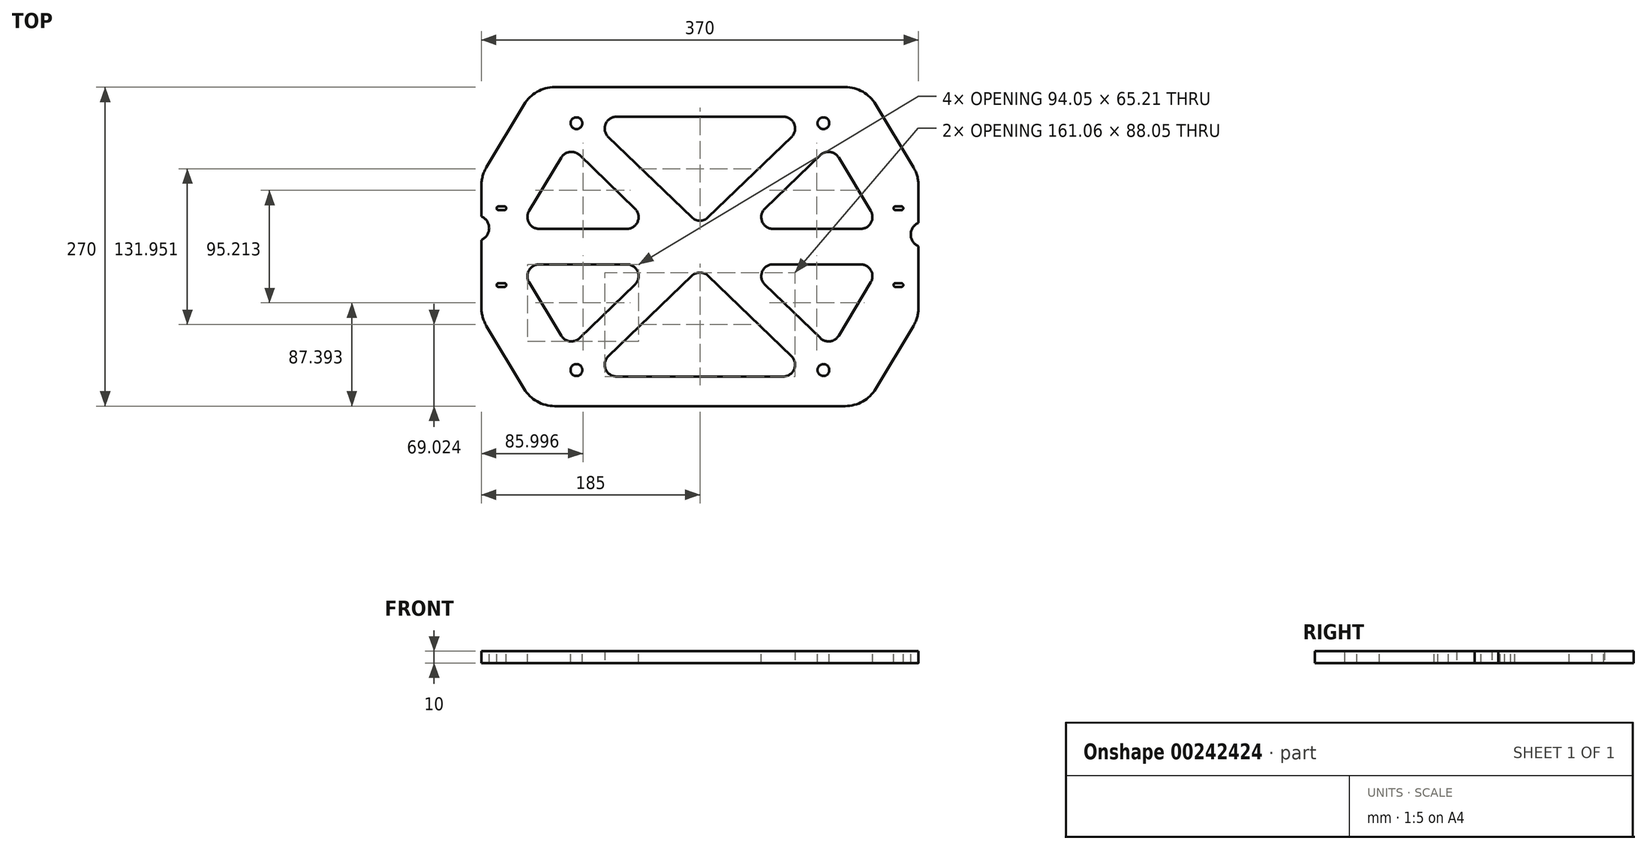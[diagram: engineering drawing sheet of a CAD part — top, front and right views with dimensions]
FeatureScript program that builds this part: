
annotation { "Feature Type Name" : "Feature", "Feature Type Description" : "" }
export const myFeature = defineFeature(function(context is Context, id is Id, definition is map)
    precondition{}
    {
        {
            var Q0;
            Q0=qCreatedBy(makeId("Top.planeOp"),FACE);
            var sketch = newSketch(context, id + "F0", { "sketchPlane" : qUnion([Q0])});
            skLineSegment(sketch, "E0.bottom", {"start": v(185, 135) * mm, "end": v(-185, 135) * mm, "construction": true});
            skLineSegment(sketch, "E0.top", {"start": v(185, -135) * mm, "end": v(-185, -135) * mm, "construction": true});
            skLineSegment(sketch, "E0.left", {"start": v(185, 135) * mm, "end": v(185, -135) * mm, "construction": true});
            skLineSegment(sketch, "E0.right", {"start": v(-185, 135) * mm, "end": v(-185, -135) * mm, "construction": true});
            skPoint(sketch, "E0.middle", {"position": v(0, 0) * mm});
            skLineSegment(sketch, "E1", {"start": v(-140, 135) * mm, "end": v(140, 135) * mm});
            skLineSegment(sketch, "E2", {"start": v(-140, -135) * mm, "end": v(140, -135) * mm});
            skLineSegment(sketch, "E3", {"start": v(-185, 60) * mm, "end": v(-185, -60) * mm});
            skLineSegment(sketch, "E4", {"start": v(185, 60) * mm, "end": v(185, -60) * mm});
            skLineSegment(sketch, "E5", {"start": v(-140, 135) * mm, "end": v(-185, 60) * mm});
            skLineSegment(sketch, "E6", {"start": v(140, 135) * mm, "end": v(185, 60) * mm});
            skLineSegment(sketch, "E7", {"start": v(140, -135) * mm, "end": v(185, -60) * mm});
            skLineSegment(sketch, "E8", {"start": v(-140, -135) * mm, "end": v(-185, -60) * mm});
            skLineSegment(sketch, "E9", {"start": v(-140, 135) * mm, "end": v(140, -135) * mm, "construction": true});
            skLineSegment(sketch, "E10", {"start": v(140, 135) * mm, "end": v(-140, -135) * mm, "construction": true});
            skLineSegment(sketch, "E11", {"start": v(-95.35, -110) * mm, "end": v(0, -18.06) * mm});
            skLineSegment(sketch, "E12", {"start": v(0, -18.06) * mm, "end": v(95.35, -110) * mm});
            skLineSegment(sketch, "E13", {"start": v(-95.35, 110) * mm, "end": v(0, 18.06) * mm});
            skLineSegment(sketch, "E14", {"start": v(0, 18.06) * mm, "end": v(95.35, 110) * mm});
            skLineSegment(sketch, "E15", {"start": v(-185, 0) * mm, "end": v(185, 0) * mm, "construction": true});
            skLineSegment(sketch, "E16", {"start": v(110.98, 86.18) * mm, "end": v(37.17, 15) * mm});
            skLineSegment(sketch, "E17", {"start": v(37.17, 15) * mm, "end": v(153.7, 15) * mm});
            skLineSegment(sketch, "E18", {"start": v(153.7, 15) * mm, "end": v(110.98, 86.18) * mm});
            skLineSegment(sketch, "E19", {"start": v(153.7, -15) * mm, "end": v(37.17, -15) * mm});
            skLineSegment(sketch, "E20", {"start": v(37.17, -15) * mm, "end": v(110.98, -86.18) * mm});
            skLineSegment(sketch, "E21", {"start": v(110.98, -86.18) * mm, "end": v(153.7, -15) * mm});
            skLineSegment(sketch, "E22", {"start": v(-110.98, 86.18) * mm, "end": v(-37.17, 15) * mm});
            skLineSegment(sketch, "E23", {"start": v(-37.17, 15) * mm, "end": v(-153.7, 15) * mm});
            skLineSegment(sketch, "E24", {"start": v(-153.7, 15) * mm, "end": v(-110.98, 86.18) * mm});
            skLineSegment(sketch, "E25", {"start": v(-153.7, -15) * mm, "end": v(-37.17, -15) * mm});
            skLineSegment(sketch, "E26", {"start": v(-37.17, -15) * mm, "end": v(-110.98, -86.18) * mm});
            skLineSegment(sketch, "E27", {"start": v(-110.98, -86.18) * mm, "end": v(-153.7, -15) * mm});
            skLineSegment(sketch, "E28", {"start": v(-95.35, 110) * mm, "end": v(95.35, 110) * mm});
            skLineSegment(sketch, "E29", {"start": v(-95.35, -110) * mm, "end": v(95.35, -110) * mm});
            skLineSegment(sketch, "E30", {"start": v(153.7, -15) * mm, "end": v(153.7, 15) * mm, "construction": true});
            skLineSegment(sketch, "E31", {"start": v(110.98, 86.18) * mm, "end": v(110.98, -86.18) * mm, "construction": true});
            skLineSegment(sketch, "E32", {"start": v(-110.98, 86.18) * mm, "end": v(-110.98, -86.18) * mm, "construction": true});
            skLineSegment(sketch, "E33", {"start": v(-153.7, 15) * mm, "end": v(-153.7, -15) * mm, "construction": true});
            skLineSegment(sketch, "E34", {"start": v(-37.17, 15) * mm, "end": v(37.17, 15) * mm, "construction": true});
            skLineSegment(sketch, "E35", {"start": v(-37.17, -15) * mm, "end": v(37.17, -15) * mm, "construction": true});
            skLineSegment(sketch, "E36", {"start": v(37.17, 15) * mm, "end": v(37.17, -15) * mm, "construction": true});
            skLineSegment(sketch, "E37", {"start": v(-37.17, 15) * mm, "end": v(-37.17, -15) * mm, "construction": true});
            skLineSegment(sketch, "E38", {"start": v(-110.98, 86.18) * mm, "end": v(110.98, 86.18) * mm, "construction": true});
            skPoint(sketch, "E39", {"position": v(0, -15) * mm});
            skLineSegment(sketch, "E40", {"start": v(95.35, 110) * mm, "end": v(95.35, -110) * mm, "construction": true});
            skLineSegment(sketch, "E41", {"start": v(-95.35, 110) * mm, "end": v(-95.35, -110) * mm, "construction": true});
            skLineSegment(sketch, "E42", {"start": v(0, 18.06) * mm, "end": v(0, -18.06) * mm, "construction": true});
            skPoint(sketch, "E43", {"position": v(-153.7, 0) * mm});
            skSolve(sketch);
        }
        {
            var Q0;
            Q0=makeQuery(id+"F0.imprint","IMPRINT",FACE,{"disambiguationData":[TD([[makeQuery(id+"F0.imprint","IMPRINT",EDGE,{"derivedFrom":sQuery(id+"F0.wireOp",EDGE,"E1")}),-1.0]])]});
            extrude(context, id + "F1", {"entities" : qUnion([Q0]), "depth" : 10 * mm});
        }
        {
            var Q0;
            Q0=makeQuery(id+"F1.opExtrude","SWEPT_EDGE",EDGE,{"disambiguationData":[OSD([sQuery(id+"F0.wireOp",EDGE,"E22"),sQuery(id+"F0.wireOp",EDGE,"E24")])]});
            var Q1;
            Q1=makeQuery(id+"F1.opExtrude","SWEPT_EDGE",EDGE,{"disambiguationData":[OSD([sQuery(id+"F0.wireOp",EDGE,"E23"),sQuery(id+"F0.wireOp",EDGE,"E24")])]});
            var Q2;
            Q2=makeQuery(id+"F1.opExtrude","SWEPT_EDGE",EDGE,{"disambiguationData":[OSD([sQuery(id+"F0.wireOp",EDGE,"E22"),sQuery(id+"F0.wireOp",EDGE,"E23")])]});
            var Q3;
            Q3=makeQuery(id+"F1.opExtrude","SWEPT_EDGE",EDGE,{"disambiguationData":[OSD([sQuery(id+"F0.wireOp",EDGE,"E17"),sQuery(id+"F0.wireOp",EDGE,"E18")])]});
            var Q4;
            Q4=makeQuery(id+"F1.opExtrude","SWEPT_EDGE",EDGE,{"disambiguationData":[OSD([sQuery(id+"F0.wireOp",EDGE,"E13"),sQuery(id+"F0.wireOp",EDGE,"E14")])]});
            var Q5;
            Q5=makeQuery(id+"F1.opExtrude","SWEPT_EDGE",EDGE,{"disambiguationData":[OSD([sQuery(id+"F0.wireOp",EDGE,"E13"),sQuery(id+"F0.wireOp",EDGE,"E28")])]});
            var Q6;
            Q6=makeQuery(id+"F1.opExtrude","SWEPT_EDGE",EDGE,{"disambiguationData":[OSD([sQuery(id+"F0.wireOp",EDGE,"E14"),sQuery(id+"F0.wireOp",EDGE,"E28")])]});
            var Q7;
            Q7=makeQuery(id+"F1.opExtrude","SWEPT_EDGE",EDGE,{"disambiguationData":[OSD([sQuery(id+"F0.wireOp",EDGE,"E25"),sQuery(id+"F0.wireOp",EDGE,"E27")])]});
            var Q8;
            Q8=makeQuery(id+"F1.opExtrude","SWEPT_EDGE",EDGE,{"disambiguationData":[OSD([sQuery(id+"F0.wireOp",EDGE,"E25"),sQuery(id+"F0.wireOp",EDGE,"E26")])]});
            var Q9;
            Q9=makeQuery(id+"F1.opExtrude","SWEPT_EDGE",EDGE,{"disambiguationData":[OSD([sQuery(id+"F0.wireOp",EDGE,"E26"),sQuery(id+"F0.wireOp",EDGE,"E27")])]});
            var Q10;
            Q10=makeQuery(id+"F1.opExtrude","SWEPT_EDGE",EDGE,{"disambiguationData":[OSD([sQuery(id+"F0.wireOp",EDGE,"E11"),sQuery(id+"F0.wireOp",EDGE,"E12")])]});
            var Q11;
            Q11=makeQuery(id+"F1.opExtrude","SWEPT_EDGE",EDGE,{"disambiguationData":[OSD([sQuery(id+"F0.wireOp",EDGE,"E11"),sQuery(id+"F0.wireOp",EDGE,"E29")])]});
            var Q12;
            Q12=makeQuery(id+"F1.opExtrude","SWEPT_EDGE",EDGE,{"disambiguationData":[OSD([sQuery(id+"F0.wireOp",EDGE,"E12"),sQuery(id+"F0.wireOp",EDGE,"E29")])]});
            var Q13;
            Q13=makeQuery(id+"F1.opExtrude","SWEPT_EDGE",EDGE,{"disambiguationData":[OSD([sQuery(id+"F0.wireOp",EDGE,"E19"),sQuery(id+"F0.wireOp",EDGE,"E21")])]});
            var Q14;
            Q14=makeQuery(id+"F1.opExtrude","SWEPT_EDGE",EDGE,{"disambiguationData":[OSD([sQuery(id+"F0.wireOp",EDGE,"E19"),sQuery(id+"F0.wireOp",EDGE,"E20")])]});
            var Q15;
            Q15=makeQuery(id+"F1.opExtrude","SWEPT_EDGE",EDGE,{"disambiguationData":[OSD([sQuery(id+"F0.wireOp",EDGE,"E20"),sQuery(id+"F0.wireOp",EDGE,"E21")])]});
            var Q16;
            Q16=makeQuery(id+"F1.opExtrude","SWEPT_EDGE",EDGE,{"disambiguationData":[OSD([sQuery(id+"F0.wireOp",EDGE,"E16"),sQuery(id+"F0.wireOp",EDGE,"E18")])]});
            var Q17;
            Q17=makeQuery(id+"F1.opExtrude","SWEPT_EDGE",EDGE,{"disambiguationData":[OSD([sQuery(id+"F0.wireOp",EDGE,"E16"),sQuery(id+"F0.wireOp",EDGE,"E17")])]});
            fillet(context, id + "F2", {"entities" : qUnion([Q0, Q1, Q2, Q3, Q4, Q5, Q6, Q7, Q8, Q9, Q10, Q11, Q12, Q13, Q14, Q15, Q16, Q17]), "radius" : 10 * mm, "tangentPropagation" : true, "allowEdgeOverflow" : false});
        }
        {
            var Q0;
            Q0=makeQuery(id+"F1.opExtrude","SWEPT_EDGE",EDGE,{"disambiguationData":[OSD([sQuery(id+"F0.wireOp",EDGE,"E3"),sQuery(id+"F0.wireOp",EDGE,"E5")])]});
            var Q1;
            Q1=makeQuery(id+"F1.opExtrude","SWEPT_EDGE",EDGE,{"disambiguationData":[OSD([sQuery(id+"F0.wireOp",EDGE,"E1"),sQuery(id+"F0.wireOp",EDGE,"E5")])]});
            var Q2;
            Q2=makeQuery(id+"F1.opExtrude","SWEPT_EDGE",EDGE,{"disambiguationData":[OSD([sQuery(id+"F0.wireOp",EDGE,"E3"),sQuery(id+"F0.wireOp",EDGE,"E8")])]});
            var Q3;
            Q3=makeQuery(id+"F1.opExtrude","SWEPT_EDGE",EDGE,{"disambiguationData":[OSD([sQuery(id+"F0.wireOp",EDGE,"E2"),sQuery(id+"F0.wireOp",EDGE,"E8")])]});
            var Q4;
            Q4=makeQuery(id+"F1.opExtrude","SWEPT_EDGE",EDGE,{"disambiguationData":[OSD([sQuery(id+"F0.wireOp",EDGE,"E2"),sQuery(id+"F0.wireOp",EDGE,"E7")])]});
            var Q5;
            Q5=makeQuery(id+"F1.opExtrude","SWEPT_EDGE",EDGE,{"disambiguationData":[OSD([sQuery(id+"F0.wireOp",EDGE,"E4"),sQuery(id+"F0.wireOp",EDGE,"E7")])]});
            var Q6;
            Q6=makeQuery(id+"F1.opExtrude","SWEPT_EDGE",EDGE,{"disambiguationData":[OSD([sQuery(id+"F0.wireOp",EDGE,"E4"),sQuery(id+"F0.wireOp",EDGE,"E6")])]});
            var Q7;
            Q7=makeQuery(id+"F1.opExtrude","SWEPT_EDGE",EDGE,{"disambiguationData":[OSD([sQuery(id+"F0.wireOp",EDGE,"E1"),sQuery(id+"F0.wireOp",EDGE,"E6")])]});
            fillet(context, id + "F3", {"entities" : qUnion([Q0, Q1, Q2, Q3, Q4, Q5, Q6, Q7]), "radius" : 30 * mm, "tangentPropagation" : true, "allowEdgeOverflow" : false});
        }
        {
            var Q0;
            Q0=makeQuery(id+"F1.opExtrude","CAP_FACE",FACE,{"disambiguationData":[OSD([sQuery(id+"F0.wireOp",EDGE,"E1"),sQuery(id+"F0.wireOp",EDGE,"E2"),sQuery(id+"F0.wireOp",EDGE,"E3"),sQuery(id+"F0.wireOp",EDGE,"E4"),sQuery(id+"F0.wireOp",EDGE,"E5"),sQuery(id+"F0.wireOp",EDGE,"E6"),sQuery(id+"F0.wireOp",EDGE,"E7"),sQuery(id+"F0.wireOp",EDGE,"E8"),sQuery(id+"F0.wireOp",EDGE,"E11"),sQuery(id+"F0.wireOp",EDGE,"E12"),sQuery(id+"F0.wireOp",EDGE,"E13"),sQuery(id+"F0.wireOp",EDGE,"E14"),sQuery(id+"F0.wireOp",EDGE,"E16"),sQuery(id+"F0.wireOp",EDGE,"E17"),sQuery(id+"F0.wireOp",EDGE,"E18"),sQuery(id+"F0.wireOp",EDGE,"E19"),sQuery(id+"F0.wireOp",EDGE,"E20"),sQuery(id+"F0.wireOp",EDGE,"E21"),sQuery(id+"F0.wireOp",EDGE,"E22"),sQuery(id+"F0.wireOp",EDGE,"E23"),sQuery(id+"F0.wireOp",EDGE,"E24"),sQuery(id+"F0.wireOp",EDGE,"E25"),sQuery(id+"F0.wireOp",EDGE,"E26"),sQuery(id+"F0.wireOp",EDGE,"E27"),sQuery(id+"F0.wireOp",EDGE,"E28"),sQuery(id+"F0.wireOp",EDGE,"E29")])],"isStart":false});
            var sketch = newSketch(context, id + "F4", { "sketchPlane" : qUnion([Q0])});
            skLineSegment(sketch, "E44.bottom", {"start": v(168, 32.5) * mm, "end": v(-168, 32.5) * mm, "construction": true});
            skLineSegment(sketch, "E44.top", {"start": v(168, -32.5) * mm, "end": v(-168, -32.5) * mm, "construction": true});
            skLineSegment(sketch, "E44.left", {"start": v(168, 32.5) * mm, "end": v(168, -32.5) * mm, "construction": true});
            skLineSegment(sketch, "E44.right", {"start": v(-168, 32.5) * mm, "end": v(-168, -32.5) * mm, "construction": true});
            skPoint(sketch, "E44.middle", {"position": v(0, 0) * mm});
            skLineSegment(sketch, "E45", {"start": v(-170.5, -32.5) * mm, "end": v(-165.5, -32.5) * mm, "construction": true});
            skPoint(sketch, "E46", {"position": v(-168, -32.5) * mm});
            skArc(sketch, "E47.0.startCap", {"start": v(-170.5, -34.1) * mm, "mid": v(-172.1, -32.5) * mm, "end": v(-170.5, -30.9) * mm});
            skArc(sketch, "E47.0.endCap", {"start": v(-165.5, -30.9) * mm, "mid": v(-163.9, -32.5) * mm, "end": v(-165.5, -34.1) * mm});
            skLineSegment(sketch, "E47.0.left", {"start": v(-170.5, -30.9) * mm, "end": v(-165.5, -30.9) * mm});
            skLineSegment(sketch, "E47.0.right", {"start": v(-170.5, -34.1) * mm, "end": v(-165.5, -34.1) * mm});
            skLineSegment(sketch, "E48", {"start": v(165.5, -32.5) * mm, "end": v(170.5, -32.5) * mm, "construction": true});
            skPoint(sketch, "E49", {"position": v(168, -32.5) * mm});
            skArc(sketch, "E50.0.startCap", {"start": v(165.5, -34.1) * mm, "mid": v(163.9, -32.5) * mm, "end": v(165.5, -30.9) * mm});
            skArc(sketch, "E50.0.endCap", {"start": v(170.5, -30.9) * mm, "mid": v(172.1, -32.5) * mm, "end": v(170.5, -34.1) * mm});
            skLineSegment(sketch, "E50.0.left", {"start": v(165.5, -30.9) * mm, "end": v(170.5, -30.9) * mm});
            skLineSegment(sketch, "E50.0.right", {"start": v(165.5, -34.1) * mm, "end": v(170.5, -34.1) * mm});
            skLineSegment(sketch, "E51", {"start": v(165.5, 32.5) * mm, "end": v(170.5, 32.5) * mm, "construction": true});
            skPoint(sketch, "E52", {"position": v(168, 32.5) * mm});
            skArc(sketch, "E53.0.startCap", {"start": v(165.5, 30.9) * mm, "mid": v(163.9, 32.5) * mm, "end": v(165.5, 34.1) * mm});
            skArc(sketch, "E53.0.endCap", {"start": v(170.5, 34.1) * mm, "mid": v(172.1, 32.5) * mm, "end": v(170.5, 30.9) * mm});
            skLineSegment(sketch, "E53.0.left", {"start": v(165.5, 34.1) * mm, "end": v(170.5, 34.1) * mm});
            skLineSegment(sketch, "E53.0.right", {"start": v(165.5, 30.9) * mm, "end": v(170.5, 30.9) * mm});
            skLineSegment(sketch, "E54", {"start": v(-170.5, 32.5) * mm, "end": v(-165.5, 32.5) * mm, "construction": true});
            skPoint(sketch, "E55", {"position": v(-168, 32.5) * mm});
            skArc(sketch, "E56.0.startCap", {"start": v(-170.5, 30.9) * mm, "mid": v(-172.1, 32.5) * mm, "end": v(-170.5, 34.1) * mm});
            skArc(sketch, "E56.0.endCap", {"start": v(-165.5, 34.1) * mm, "mid": v(-163.9, 32.5) * mm, "end": v(-165.5, 30.9) * mm});
            skLineSegment(sketch, "E56.0.left", {"start": v(-170.5, 34.1) * mm, "end": v(-165.5, 34.1) * mm});
            skLineSegment(sketch, "E56.0.right", {"start": v(-170.5, 30.9) * mm, "end": v(-165.5, 30.9) * mm});
            skSolve(sketch);
        }
        {
            var Q0;
            Q0 = qSketchRegion(id + "F4", true);
            extrude(context, id + "F5", {"entities" : qUnion([Q0]), "operationType" : NewBodyOperationType.REMOVE, "endBound" : BoundingType.THROUGH_ALL, "oppositeDirection" : true, "depth" : 25 * mm});
        }
        {
            var Q0;
            Q0=makeQuery(id+"F1.opExtrude","CAP_FACE",FACE,{"disambiguationData":[OSD([sQuery(id+"F0.wireOp",EDGE,"E1"),sQuery(id+"F0.wireOp",EDGE,"E2"),sQuery(id+"F0.wireOp",EDGE,"E3"),sQuery(id+"F0.wireOp",EDGE,"E4"),sQuery(id+"F0.wireOp",EDGE,"E5"),sQuery(id+"F0.wireOp",EDGE,"E6"),sQuery(id+"F0.wireOp",EDGE,"E7"),sQuery(id+"F0.wireOp",EDGE,"E8"),sQuery(id+"F0.wireOp",EDGE,"E11"),sQuery(id+"F0.wireOp",EDGE,"E12"),sQuery(id+"F0.wireOp",EDGE,"E13"),sQuery(id+"F0.wireOp",EDGE,"E14"),sQuery(id+"F0.wireOp",EDGE,"E16"),sQuery(id+"F0.wireOp",EDGE,"E17"),sQuery(id+"F0.wireOp",EDGE,"E18"),sQuery(id+"F0.wireOp",EDGE,"E19"),sQuery(id+"F0.wireOp",EDGE,"E20"),sQuery(id+"F0.wireOp",EDGE,"E21"),sQuery(id+"F0.wireOp",EDGE,"E22"),sQuery(id+"F0.wireOp",EDGE,"E23"),sQuery(id+"F0.wireOp",EDGE,"E24"),sQuery(id+"F0.wireOp",EDGE,"E25"),sQuery(id+"F0.wireOp",EDGE,"E26"),sQuery(id+"F0.wireOp",EDGE,"E27"),sQuery(id+"F0.wireOp",EDGE,"E28"),sQuery(id+"F0.wireOp",EDGE,"E29")])],"isStart":false});
            var sketch = newSketch(context, id + "F6", { "sketchPlane" : qUnion([Q0])});
            skLineSegment(sketch, "E57.bottom", {"start": v(104.5, 104.5) * mm, "end": v(-104.5, 104.5) * mm, "construction": true});
            skLineSegment(sketch, "E57.top", {"start": v(104.5, -104.5) * mm, "end": v(-104.5, -104.5) * mm, "construction": true});
            skLineSegment(sketch, "E57.left", {"start": v(104.5, 104.5) * mm, "end": v(104.5, -104.5) * mm, "construction": true});
            skLineSegment(sketch, "E57.right", {"start": v(-104.5, 104.5) * mm, "end": v(-104.5, -104.5) * mm, "construction": true});
            skPoint(sketch, "E57.middle", {"position": v(0, 0) * mm});
            skCircle(sketch, "E58", {"center": v(-104.5, 104.5) * mm, "radius": 5 * mm});
            skCircle(sketch, "E59", {"center": v(104.5, 104.5) * mm, "radius": 5 * mm});
            skCircle(sketch, "E60", {"center": v(-104.5, -104.5) * mm, "radius": 5 * mm});
            skCircle(sketch, "E61", {"center": v(104.5, -104.5) * mm, "radius": 5 * mm});
            skSolve(sketch);
        }
        {
            var Q0;
            Q0 = qSketchRegion(id + "F6", true);
            extrude(context, id + "F7", {"entities" : qUnion([Q0]), "operationType" : NewBodyOperationType.REMOVE, "endBound" : BoundingType.THROUGH_ALL, "oppositeDirection" : true, "depth" : 25 * mm});
        }
        {
            var Q0;
            Q0=makeQuery(id+"F1.opExtrude","CAP_FACE",FACE,{"disambiguationData":[OSD([sQuery(id+"F0.wireOp",EDGE,"E1"),sQuery(id+"F0.wireOp",EDGE,"E2"),sQuery(id+"F0.wireOp",EDGE,"E3"),sQuery(id+"F0.wireOp",EDGE,"E4"),sQuery(id+"F0.wireOp",EDGE,"E5"),sQuery(id+"F0.wireOp",EDGE,"E6"),sQuery(id+"F0.wireOp",EDGE,"E7"),sQuery(id+"F0.wireOp",EDGE,"E8"),sQuery(id+"F0.wireOp",EDGE,"E11"),sQuery(id+"F0.wireOp",EDGE,"E12"),sQuery(id+"F0.wireOp",EDGE,"E13"),sQuery(id+"F0.wireOp",EDGE,"E14"),sQuery(id+"F0.wireOp",EDGE,"E16"),sQuery(id+"F0.wireOp",EDGE,"E17"),sQuery(id+"F0.wireOp",EDGE,"E18"),sQuery(id+"F0.wireOp",EDGE,"E19"),sQuery(id+"F0.wireOp",EDGE,"E20"),sQuery(id+"F0.wireOp",EDGE,"E21"),sQuery(id+"F0.wireOp",EDGE,"E22"),sQuery(id+"F0.wireOp",EDGE,"E23"),sQuery(id+"F0.wireOp",EDGE,"E24"),sQuery(id+"F0.wireOp",EDGE,"E25"),sQuery(id+"F0.wireOp",EDGE,"E26"),sQuery(id+"F0.wireOp",EDGE,"E27"),sQuery(id+"F0.wireOp",EDGE,"E28"),sQuery(id+"F0.wireOp",EDGE,"E29")])],"isStart":false});
            var sketch = newSketch(context, id + "F8", { "sketchPlane" : qUnion([Q0])});
            skArc(sketch, "E62", {"start": v(-185, 5.64) * mm, "mid": v(-178.44, 15.64) * mm, "end": v(-185, 25.64) * mm});
            skArc(sketch, "E63", {"start": v(185, 20.26) * mm, "mid": v(178.44, 10.26) * mm, "end": v(185, 0.26) * mm});
            skSolve(sketch);
        }
        {
            var Q0;
            {var subQ0=sQuery(id+"F8.wireOp",EDGE,"E62");Q0=makeQuery(id+"F8.imprint","IMPRINT",FACE,{"disambiguationData":[TD([[makeQuery(id+"F8.imprint","IMPRINT",EDGE,{"derivedFrom":subQ0}),1.0]])]});}
            var Q1;
            {var subQ0=sQuery(id+"F8.wireOp",EDGE,"E63");Q1=makeQuery(id+"F8.imprint","IMPRINT",FACE,{"disambiguationData":[TD([[makeQuery(id+"F8.imprint","IMPRINT",EDGE,{"derivedFrom":subQ0}),1.0]])]});}
            extrude(context, id + "F9", {"entities" : qUnion([Q0, Q1]), "operationType" : NewBodyOperationType.REMOVE, "endBound" : BoundingType.THROUGH_ALL, "oppositeDirection" : true, "depth" : 25 * mm});
        }
    });
